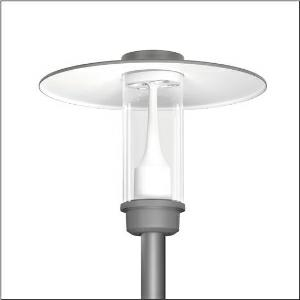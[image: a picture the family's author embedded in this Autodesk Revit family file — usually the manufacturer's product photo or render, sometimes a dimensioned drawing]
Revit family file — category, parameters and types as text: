
# Revit family: litepole_2_iq___p1_0a_5xa5425ff14hp_8674
name_source: partatom
category: Lighting Fixtures
units: mm (PartAtom-declared; Revit-internal decimal feet)

## family parameters
Cut with Voids When Loaded = No
Host = Face
Light Source = No
Part Type = Normal
Room Calculation Point = No
Round Connector Dimension = Use Diameter
Shared = No

## types (1)
- --- (1 x LED, 4730 lm, 33.6 W, 3000K)
    Apparent Load = 34 VA
    CIE Flux Codes = 32 62 90 96 100
    Color Rendering = 70
    Color Temperature = 3000K
    Default Elevation = 1800 mm
    Description = Litepole 2 iQ, mast luminaire, Module 540 iQ-SR, primary light control with 3 zone facetted reflector, of plastic, silver coated, highly specular, structured, primary optical cover: cover, of PMMA, transparent, light distribution: P1.0a, light emission: direct distribution, primary light characteristic: strongly asymmetric, installation type: post-top, LED, High Power LED, rated luminous flux: 4.730lm, luminous efficacy: 141lm/W, light colour: 730, colour temperature: 3000K, control gear: iQ Street-Remote, control: pre-setting: logarithmic dimming characteristic, Street-Remote, Auto-Match, Temp-Guard, Lumen-Switch, Night-Set, Smart-Wire, Light-Fading, Desk-Remote (wireless, voltage-free reading and setting of iQ features in the workshop via application-optimized NFC function/RFID function), optimised constant luminous flux control (CLO 2.0), with terminal, 6-pole, max. 2.5mm², mains connection: 230..240V, AC, 50/60Hz, start of lifetime: 34W, end of service life: 36W, reduction: 15W, luminaire housing, upper part, of aluminium, coated, Siteco® metallic grey (DB 702S), diameter: 750mm, height: 590mm, spigot size: d x l = 76 x 70mm (post-top) | with reducer (optional accessory) 60 x 70mm, mounting height: 3..5m, post-top mast mounting element, of diecast aluminium, coated, Siteco® metallic grey (DB 702S), Module 540 iQ-SR, traffic white (RAL 9016), equipment: Power, protection rating (complete): IP65, insulation class (complete): insulation class II (safety insulation), certification: CE, ENEC, VDE, packaging unit: 1 piece

Light Distribution: P1.0a
    Height = 590 mm
    Lamp = 1 x LED
    Lamp Light Flux = 4730 lm
    Lamp Power = 33.6 W
    Lamp count = 1
    Length = 750 mm
    Luminous efficacy = 141 lm/W
    Manufacturer = Siteco
    ModVariant = No
    Model = 5XA5425FF14HP
    Number of Poles = 1
    OnlyDefault = Yes
    Power Factor = 1
    Product Name = Litepole 2 iQ | P1.0a
    Product group = mast luminaire | pylon top
    ProductGroupID = 6100
    Protection Class = Protection class II
    Protection Degree = IP 65
    RLX_Detail_Level = 1
    RLX_Emergency_Light_Flux = 0 lm
    RLX_Emergency_Type = 0
    RLX_Emergency_Type_DB = No
    RlxData = <blob elided: 32129 chars, md5=c24722cc>
    Socket = socket
    Standby Power = 0 W
    System Light Flux = 4730 lm
    System Power = 34 W
    Type Comments = factory setting: luminous flux: 100 % | dim-lin: 254 | 695 mA
    Type Image = l_1006518.jpg
    URL = http://relux.com
    VarID = @adj_192372
    Voltage = 0 V
    Weight = 0.00 kg
    Width = 0 mm  [stored 0 ft]

note: [stored X ft] marks values corroborated as IEEE doubles in the binary element streams (Revit-internal decimal feet)

## geometry (parser evidence)
native form markers: Blend x4, Sweep x11
no freeform markers — native parametric forms only
